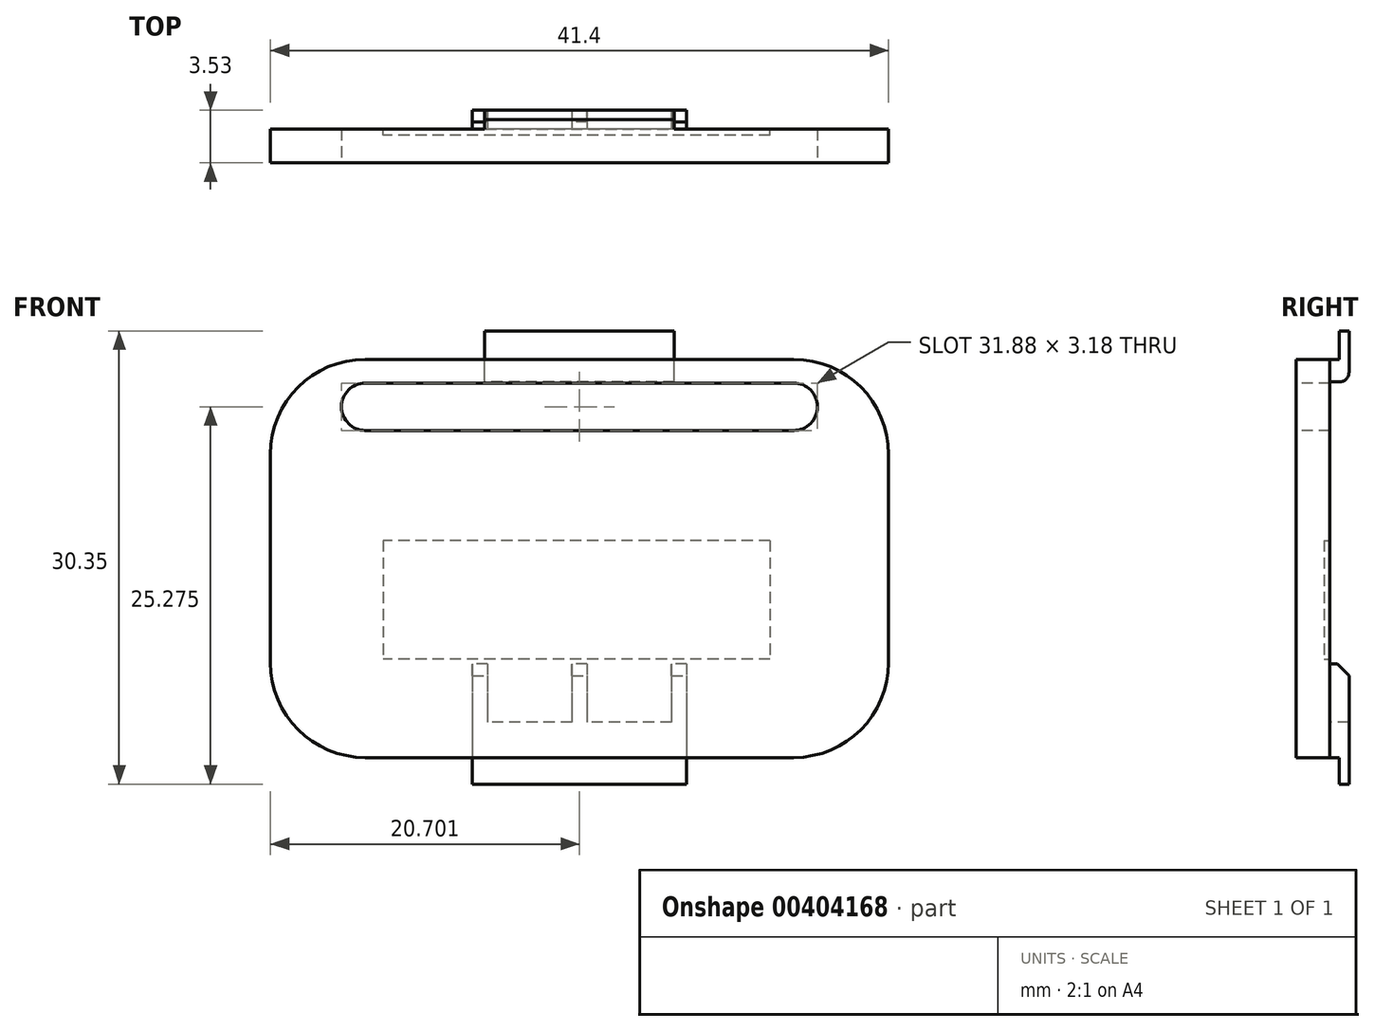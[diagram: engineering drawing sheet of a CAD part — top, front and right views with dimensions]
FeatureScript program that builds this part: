
annotation { "Feature Type Name" : "Feature", "Feature Type Description" : "" }
export const myFeature = defineFeature(function(context is Context, id is Id, definition is map)
    precondition{}
    {
        {
            var Q0;
            Q0=qCreatedBy(makeId("Front.planeOp"),FACE);
            var sketch = newSketch(context, id + "F0", { "sketchPlane" : qUnion([Q0])});
            skLineSegment(sketch, "E0", {"start": v(0, 0) * mm, "end": v(0, 650.6) * mm, "construction": true});
            skLineSegment(sketch, "E1", {"start": v(0, 0) * mm, "end": v(978.54, 0) * mm, "construction": true});
            skLineSegment(sketch, "E2.bottom", {"start": v(6.35, 0) * mm, "end": v(35.05, 0) * mm});
            skLineSegment(sketch, "E2.top", {"start": v(6.35, 26.67) * mm, "end": v(35.05, 26.67) * mm});
            skLineSegment(sketch, "E2.left", {"start": v(0, 6.35) * mm, "end": v(0, 20.32) * mm});
            skLineSegment(sketch, "E2.right", {"start": v(41.4, 6.35) * mm, "end": v(41.4, 20.32) * mm});
            skPoint(sketch, "E3.visualSharp", {"position": v(0, 26.67) * mm});
            skArc(sketch, "E3.filletArc", {"start": v(6.35, 26.67) * mm, "mid": v(1.86, 24.81) * mm, "end": v(0, 20.32) * mm});
            skPoint(sketch, "E4.visualSharp", {"position": v(41.4, 26.67) * mm});
            skArc(sketch, "E4.filletArc", {"start": v(41.4, 20.32) * mm, "mid": v(39.54, 24.81) * mm, "end": v(35.05, 26.67) * mm});
            skPoint(sketch, "E5.visualSharp", {"position": v(41.4, 0) * mm});
            skArc(sketch, "E5.filletArc", {"start": v(35.05, 0) * mm, "mid": v(39.54, 1.86) * mm, "end": v(41.4, 6.35) * mm});
            skPoint(sketch, "E6.visualSharp", {"position": v(0, 0) * mm});
            skArc(sketch, "E6.filletArc", {"start": v(0, 6.35) * mm, "mid": v(1.86, 1.86) * mm, "end": v(6.35, 0) * mm});
            skSolve(sketch);
        }
        {
            var Q0;
            Q0=makeQuery(id+"F0.imprint","IMPRINT",FACE,{"disambiguationData":[TD([[makeQuery(id+"F0.imprint","IMPRINT",EDGE,{"derivedFrom":sQuery(id+"F0.wireOp",EDGE,"E2.bottom")}),1.0]])]});
            extrude(context, id + "F1", {"entities" : qUnion([Q0]), "oppositeDirection" : true, "depth" : 2.26 * mm});
        }
        {
            var Q0;
            Q0=makeQuery(id+"F1.opExtrude","CAP_FACE",FACE,{"disambiguationData":[OSD([sQuery(id+"F0.wireOp",EDGE,"E2.bottom"),sQuery(id+"F0.wireOp",EDGE,"E2.top"),sQuery(id+"F0.wireOp",EDGE,"E2.left"),sQuery(id+"F0.wireOp",EDGE,"E2.right"),sQuery(id+"F0.wireOp",EDGE,"E3.filletArc"),sQuery(id+"F0.wireOp",EDGE,"E4.filletArc"),sQuery(id+"F0.wireOp",EDGE,"E5.filletArc"),sQuery(id+"F0.wireOp",EDGE,"E6.filletArc")])],"isStart":false});
            var sketch = newSketch(context, id + "F2", { "sketchPlane" : qUnion([Q0])});
            skLineSegment(sketch, "E7.bottom", {"start": v(-33.46, 14.54) * mm, "end": v(-7.53, 14.54) * mm});
            skLineSegment(sketch, "E7.top", {"start": v(-33.46, 6.6) * mm, "end": v(-7.53, 6.6) * mm});
            skLineSegment(sketch, "E7.left", {"start": v(-33.46, 14.54) * mm, "end": v(-33.46, 6.6) * mm});
            skLineSegment(sketch, "E7.right", {"start": v(-7.53, 14.54) * mm, "end": v(-7.53, 6.6) * mm});
            skLineSegment(sketch, "E8", {"start": v(-20.7, 36.85) * mm, "end": v(-20.7, -12.43) * mm, "construction": true});
            skSolve(sketch);
        }
        {
            var Q0;
            Q0=makeQuery(id+"F2.imprint","IMPRINT",FACE,{"disambiguationData":[TD([[makeQuery(id+"F2.imprint","IMPRINT",EDGE,{"derivedFrom":sQuery(id+"F2.wireOp",EDGE,"E7.bottom")}),-1.0]])]});
            extrude(context, id + "F3", {"entities" : qUnion([Q0]), "operationType" : NewBodyOperationType.REMOVE, "oppositeDirection" : true, "depth" : 0.4 * mm});
        }
        {
            var Q0;
            Q0=makeQuery(id+"F2.imprint","IMPRINT",FACE,{"disambiguationData":[TD([[makeQuery(id+"F2.imprint","IMPRINT",EDGE,{"derivedFrom":sQuery(id+"F2.wireOp",EDGE,"E7.bottom")}),1.0]])]});
            var sketch = newSketch(context, id + "F4", { "sketchPlane" : qUnion([Q0])});
            skLineSegment(sketch, "E9.top", {"start": v(-26.86, 2.38) * mm, "end": v(-21.2, 2.38) * mm});
            skLineSegment(sketch, "E9.left", {"start": v(-26.86, 6.29) * mm, "end": v(-26.86, 2.38) * mm});
            skLineSegment(sketch, "E9.right", {"start": v(-14.54, 6.29) * mm, "end": v(-14.54, 2.38) * mm});
            skLineSegment(sketch, "E10", {"start": v(-27.88, 6.29) * mm, "end": v(-27.88, -1.78) * mm});
            skLineSegment(sketch, "E11", {"start": v(-13.53, 6.29) * mm, "end": v(-13.53, -1.78) * mm});
            skLineSegment(sketch, "E12", {"start": v(-27.88, -1.78) * mm, "end": v(-13.53, -1.78) * mm});
            skLineSegment(sketch, "E13", {"start": v(-20.2, 6.29) * mm, "end": v(-20.2, 2.38) * mm});
            skLineSegment(sketch, "E14", {"start": v(-21.2, 6.29) * mm, "end": v(-21.2, 2.38) * mm});
            skLineSegment(sketch, "E15.trimOffspring", {"start": v(-20.2, 2.38) * mm, "end": v(-14.54, 2.38) * mm});
            skLineSegment(sketch, "E16", {"start": v(-14.54, 6.29) * mm, "end": v(-13.53, 6.29) * mm});
            skLineSegment(sketch, "E17", {"start": v(-21.2, 6.29) * mm, "end": v(-20.2, 6.29) * mm});
            skLineSegment(sketch, "E18", {"start": v(-27.88, 6.29) * mm, "end": v(-26.86, 6.29) * mm});
            skSolve(sketch);
        }
        {
            var Q0;
            {var subQ0=sQuery(id+"F4.wireOp",EDGE,"E12");Q0=makeQuery(id+"F4.imprint","IMPRINT",FACE,{"disambiguationData":[TD([[makeQuery(id+"F4.imprint","IMPRINT",EDGE,{"derivedFrom":subQ0}),1.0]])]});}
            var Q1;
            Q1=makeQuery(id+"F4.imprint","IMPRINT",FACE,{"disambiguationData":[TD([[makeQuery(id+"F4.imprint","IMPRINT",EDGE,{"derivedFrom":sQuery(id+"F4.wireOp",EDGE,"E9.top")}),-1.0]])]});
            extrude(context, id + "F5", {"entities" : qUnion([Q0, Q1]), "operationType" : NewBodyOperationType.ADD, "depth" : 1.27 * mm});
        }
        {
            var Q0;
            Q0=makeQuery(id+"F5.opExtrude","CAP_EDGE",EDGE,{"disambiguationData":[OSD([sQuery(id+"F4.wireOp",EDGE,"E18")])],"isStart":false});
            var Q1;
            Q1=makeQuery(id+"F5.opExtrude","CAP_EDGE",EDGE,{"disambiguationData":[OSD([sQuery(id+"F4.wireOp",EDGE,"E17")])],"isStart":false});
            var Q2;
            Q2=makeQuery(id+"F5.opExtrude","CAP_EDGE",EDGE,{"disambiguationData":[OSD([sQuery(id+"F4.wireOp",EDGE,"E16")])],"isStart":false});
            chamfer(context, id + "F6", {"entities" : qUnion([Q0, Q1, Q2]), "width" : 0.8 * mm, "tangentPropagation" : true});
        }
        {
            var Q0;
            Q0=makeQuery(id+"F1.opExtrude","CAP_EDGE",EDGE,{"disambiguationData":[OSD([sQuery(id+"F0.wireOp",EDGE,"E2.top")])],"isStart":false});
            cPoint(context, id + "F7", {"entities" : qUnion([Q0]), "parameter" : 0.5});
        }
        {
            var Q0;
            Q0 = qCreatedBy(id + "F7" ,VERTEX);
            var Q1;
            Q1=makeQuery(id+"F1.opExtrude","CAP_EDGE",EDGE,{"disambiguationData":[OSD([sQuery(id+"F0.wireOp",EDGE,"E2.top")])],"isStart":false});
            cPlane(context, id + "F8", {"entities" : qUnion([Q0, Q1]), "cplaneType" : CPlaneType.LINE_POINT, "offset" : 25.4 * mm, "width" : 152.4 * mm, "height" : 152.4 * mm});
        }
        {
            var Q0;
            Q0=qCreatedBy(makeId("Front.planeOp"),FACE);
            var sketch = newSketch(context, id + "F9", { "sketchPlane" : qUnion([Q0])});
            skLineSegment(sketch, "E19", {"start": v(36.64, 32.12) * mm, "end": v(36.64, -3.77) * mm, "construction": true});
            skLineSegment(sketch, "E20", {"start": v(4.76, 33.95) * mm, "end": v(4.76, -13.1) * mm, "construction": true});
            skLineSegment(sketch, "E21", {"start": v(36.64, 23.5) * mm, "end": v(4.76, 23.5) * mm, "construction": true});
            skPoint(sketch, "E22", {"position": v(35.05, 23.5) * mm});
            skPoint(sketch, "E23", {"position": v(6.35, 23.5) * mm});
            skArc(sketch, "E24", {"start": v(35.05, 21.9) * mm, "mid": v(36.64, 23.5) * mm, "end": v(35.05, 25.08) * mm});
            skArc(sketch, "E25", {"start": v(6.35, 25.08) * mm, "mid": v(4.76, 23.5) * mm, "end": v(6.35, 21.9) * mm});
            skLineSegment(sketch, "E26", {"start": v(35.05, 25.08) * mm, "end": v(6.35, 25.08) * mm});
            skLineSegment(sketch, "E27", {"start": v(35.05, 21.9) * mm, "end": v(6.35, 21.9) * mm});
            skSolve(sketch);
        }
        {
            var Q0;
            Q0 = qSketchRegion(id + "F9", true);
            extrude(context, id + "F10", {"entities" : qUnion([Q0]), "operationType" : NewBodyOperationType.REMOVE, "endBound" : BoundingType.UP_TO_NEXT, "oppositeDirection" : true, "depth" : 25.4 * mm});
        }
        {
            var Q0;
            Q0=qCreatedBy(id+"F8.planeOp",FACE);
            var sketch = newSketch(context, id + "F11", { "sketchPlane" : qUnion([Q0])});
            skLineSegment(sketch, "E28.0.1", {"start": v(0, 26.67) * mm, "end": v(2.26, 26.67) * mm, "construction": true});
            skLineSegment(sketch, "E29.1.1", {"start": v(2.26, 6.29) * mm, "end": v(2.26, 0) * mm});
            skLineSegment(sketch, "E29.1.3", {"start": v(2.26, 0) * mm, "end": v(2.26, 6.35) * mm});
            skLineSegment(sketch, "E29.1.4", {"start": v(2.26, 6.35) * mm, "end": v(2.26, 20.32) * mm});
            skLineSegment(sketch, "E29.1.5", {"start": v(2.26, 20.32) * mm, "end": v(2.26, 26.67) * mm});
            skLineSegment(sketch, "E29.1.7", {"start": v(2.26, 26.67) * mm, "end": v(2.26, 20.32) * mm, "construction": true});
            skLineSegment(sketch, "E29.1.8", {"start": v(2.26, 20.32) * mm, "end": v(2.26, 6.35) * mm});
            skLineSegment(sketch, "E29.1.9", {"start": v(2.26, 6.35) * mm, "end": v(2.26, 0) * mm});
            skLineSegment(sketch, "E29.1.11", {"start": v(2.26, 0) * mm, "end": v(2.26, 6.29) * mm});
            skLineSegment(sketch, "E29.1.13", {"start": v(2.26, 6.29) * mm, "end": v(2.26, 2.38) * mm});
            skLineSegment(sketch, "E29.1.15", {"start": v(2.26, 2.38) * mm, "end": v(2.26, 6.29) * mm});
            skLineSegment(sketch, "E29.1.17", {"start": v(2.26, 6.29) * mm, "end": v(2.26, 2.38) * mm});
            skLineSegment(sketch, "E29.1.19", {"start": v(2.26, 2.38) * mm, "end": v(2.26, 6.29) * mm});
            skLineSegment(sketch, "E30.bottom", {"start": v(2.26, 26.67) * mm, "end": v(3.53, 26.67) * mm, "construction": true});
            skLineSegment(sketch, "E30.top", {"start": v(2.9, 28.58) * mm, "end": v(3.53, 28.58) * mm});
            skLineSegment(sketch, "E30.left", {"start": v(2.26, 26.67) * mm, "end": v(2.26, 28.58) * mm, "construction": true});
            skLineSegment(sketch, "E30.right", {"start": v(3.53, 26.67) * mm, "end": v(3.53, 28.58) * mm});
            skLineSegment(sketch, "E31", {"start": v(2.26, 25.16) * mm, "end": v(2.9, 25.16) * mm});
            skLineSegment(sketch, "E32", {"start": v(3.53, 25.8) * mm, "end": v(3.53, 26.67) * mm});
            skPoint(sketch, "E33.visualSharp", {"position": v(3.53, 25.16) * mm});
            skArc(sketch, "E33.filletArc", {"start": v(2.9, 25.16) * mm, "mid": v(3.34, 25.35) * mm, "end": v(3.53, 25.8) * mm});
            skLineSegment(sketch, "E34", {"start": v(2.9, 28.58) * mm, "end": v(2.9, 26.67) * mm});
            skLineSegment(sketch, "E35", {"start": v(2.9, 26.67) * mm, "end": v(2.26, 26.67) * mm});
            skSolve(sketch);
        }
        {
            var Q0;
            Q0=makeQuery(id+"F11.imprint","IMPRINT",FACE,{"disambiguationData":[TD([[makeQuery(id+"F11.imprint","IMPRINT",EDGE,{"derivedFrom":sQuery(id+"F11.wireOp",EDGE,"h6mBb4qY-ToM4-AbI5-YBhh-zkzsSD2ylbUo.bottom")}),-1.0]])]});
            var Q1;
            Q1=makeQuery(id+"F11.imprint","IMPRINT",FACE,{"disambiguationData":[TD([[makeQuery(id+"F11.imprint","IMPRINT",EDGE,{"derivedFrom":sQuery(id+"F11.wireOp",EDGE,"E30.top")}),-1.0]])]});
            extrude(context, id + "F12", {"entities" : qUnion([Q0, Q1]), "operationType" : NewBodyOperationType.ADD, "endBound" : BoundingType.SYMMETRIC, "depth" : 12.7 * mm});
        }
        {
            var Q0;
            Q0=makeQuery(id+"F5.opExtrude","SWEPT_FACE",FACE,{"disambiguationData":[OSD([sQuery(id+"F4.wireOp",EDGE,"E11")])]});
            var sketch = newSketch(context, id + "F13", { "sketchPlane" : qUnion([Q0])});
            skLineSegment(sketch, "E36.bottom", {"start": v(-2.26, 0) * mm, "end": v(-2.9, 0) * mm});
            skLineSegment(sketch, "E36.top", {"start": v(-2.26, -1.78) * mm, "end": v(-2.9, -1.78) * mm});
            skLineSegment(sketch, "E36.left", {"start": v(-2.26, 0) * mm, "end": v(-2.26, -1.78) * mm});
            skLineSegment(sketch, "E36.right", {"start": v(-2.9, 0) * mm, "end": v(-2.9, -1.78) * mm});
            skSolve(sketch);
        }
        {
            var Q0;
            Q0=makeQuery(id+"F13.imprint","IMPRINT",FACE,{"disambiguationData":[TD([[makeQuery(id+"F13.imprint","IMPRINT",EDGE,{"derivedFrom":sQuery(id+"F13.wireOp",EDGE,"E36.bottom")}),1.0]])]});
            extrude(context, id + "F14", {"entities" : qUnion([Q0]), "operationType" : NewBodyOperationType.REMOVE, "endBound" : BoundingType.THROUGH_ALL, "oppositeDirection" : true, "depth" : 25.4 * mm});
        }
    });
